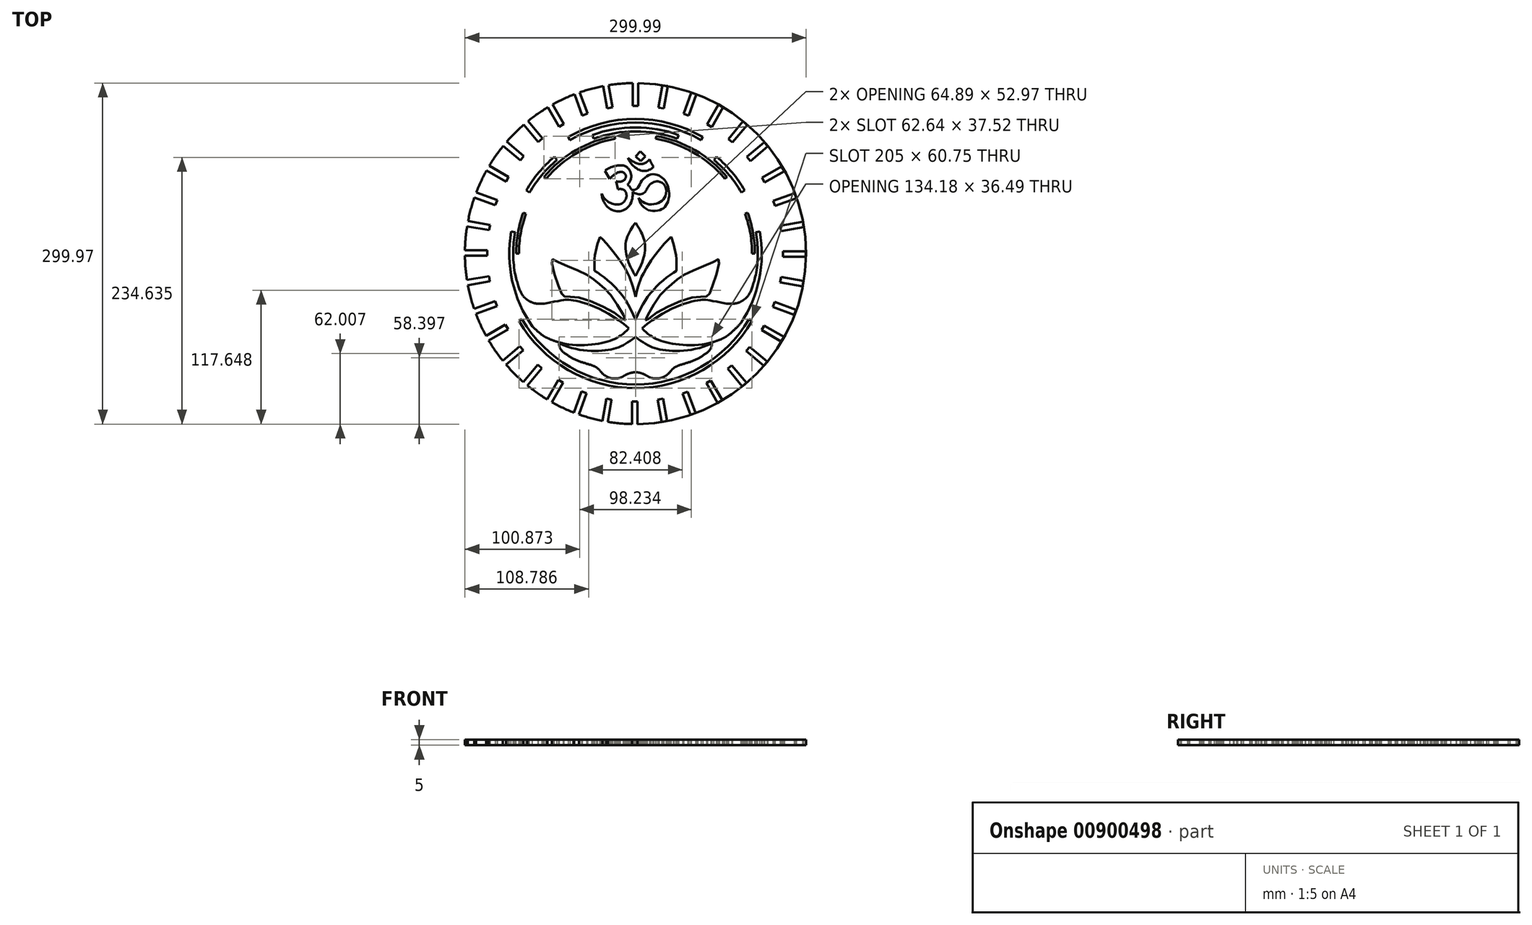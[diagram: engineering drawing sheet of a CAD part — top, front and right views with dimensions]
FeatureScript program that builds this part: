
annotation { "Feature Type Name" : "Feature", "Feature Type Description" : "" }
export const myFeature = defineFeature(function(context is Context, id is Id, definition is map)
    precondition{}
    {
        {
            var Q0;
            Q0=qCreatedBy(makeId("Top.planeOp"),FACE);
            var sketch = newSketch(context, id + "F0", { "sketchPlane" : qUnion([Q0])});
            skCircle(sketch, "E0", {"center": v(0, 0) * mm, "radius": 150 * mm});
            skLineSegment(sketch, "E1", {"start": v(0, 0) * mm, "end": v(0, 150) * mm});
            skPoint(sketch, "E2", {"position": v(0, 150) * mm});
            skPoint(sketch, "E3", {"position": v(0, 130) * mm});
            skLineSegment(sketch, "E4", {"start": v(-2.38, 130) * mm, "end": v(2.38, 130) * mm});
            skLineSegment(sketch, "E5", {"start": v(-2.38, 150) * mm, "end": v(2.37, 150) * mm});
            skLineSegment(sketch, "E6", {"start": v(-2.38, 150) * mm, "end": v(-2.38, 130) * mm});
            skLineSegment(sketch, "E7", {"start": v(2.38, 150) * mm, "end": v(2.38, 130) * mm});
            skLineSegment(sketch, "E8.1.0", {"start": v(-28.4, 147.38) * mm, "end": v(-24.92, 127.68) * mm});
            skLineSegment(sketch, "E8.1.1", {"start": v(-23.71, 148.2) * mm, "end": v(-20.24, 128.5) * mm});
            skLineSegment(sketch, "E8.1.2", {"start": v(-28.4, 147.38) * mm, "end": v(-23.71, 148.2) * mm});
            skLineSegment(sketch, "E8.1.3", {"start": v(-24.92, 127.68) * mm, "end": v(-20.24, 128.5) * mm});
            skLineSegment(sketch, "E8.2.0", {"start": v(-53.56, 140.27) * mm, "end": v(-46.72, 121.48) * mm});
            skLineSegment(sketch, "E8.2.1", {"start": v(-49.1, 141.9) * mm, "end": v(-42.25, 123.1) * mm});
            skLineSegment(sketch, "E8.2.2", {"start": v(-53.56, 140.27) * mm, "end": v(-49.1, 141.9) * mm});
            skLineSegment(sketch, "E8.2.3", {"start": v(-46.72, 121.48) * mm, "end": v(-42.25, 123.1) * mm});
            skLineSegment(sketch, "E8.3.0", {"start": v(-77.1, 128.91) * mm, "end": v(-67.1, 111.6) * mm});
            skLineSegment(sketch, "E8.3.1", {"start": v(-73, 131.29) * mm, "end": v(-63, 113.97) * mm});
            skLineSegment(sketch, "E8.3.2", {"start": v(-77.1, 128.91) * mm, "end": v(-73, 131.29) * mm});
            skLineSegment(sketch, "E8.3.3", {"start": v(-67.1, 111.6) * mm, "end": v(-63, 113.97) * mm});
            skLineSegment(sketch, "E8.4.0", {"start": v(-98.33, 113.63) * mm, "end": v(-85.47, 98.3) * mm});
            skLineSegment(sketch, "E8.4.1", {"start": v(-94.69, 116.68) * mm, "end": v(-81.83, 101.36) * mm});
            skLineSegment(sketch, "E8.4.2", {"start": v(-98.33, 113.63) * mm, "end": v(-94.69, 116.68) * mm});
            skLineSegment(sketch, "E8.4.3", {"start": v(-85.47, 98.3) * mm, "end": v(-81.83, 101.36) * mm});
            skLineSegment(sketch, "E8.5.0", {"start": v(-116.57, 94.9) * mm, "end": v(-101.25, 82.04) * mm});
            skLineSegment(sketch, "E8.5.1", {"start": v(-113.52, 98.54) * mm, "end": v(-98.2, 85.68) * mm});
            skLineSegment(sketch, "E8.5.2", {"start": v(-116.57, 94.9) * mm, "end": v(-113.52, 98.54) * mm});
            skLineSegment(sketch, "E8.5.3", {"start": v(-101.25, 82.04) * mm, "end": v(-98.2, 85.68) * mm});
            skLineSegment(sketch, "E8.6.0", {"start": v(-131.29, 73.28) * mm, "end": v(-113.97, 63.28) * mm});
            skLineSegment(sketch, "E8.6.1", {"start": v(-128.91, 77.4) * mm, "end": v(-111.6, 67.4) * mm});
            skLineSegment(sketch, "E8.6.2", {"start": v(-131.29, 73.28) * mm, "end": v(-128.91, 77.4) * mm});
            skLineSegment(sketch, "E8.6.3", {"start": v(-113.97, 63.28) * mm, "end": v(-111.6, 67.4) * mm});
            skLineSegment(sketch, "E8.7.0", {"start": v(-142.02, 49.44) * mm, "end": v(-123.23, 42.6) * mm});
            skLineSegment(sketch, "E8.7.1", {"start": v(-140.4, 53.9) * mm, "end": v(-121.6, 47.06) * mm});
            skLineSegment(sketch, "E8.7.2", {"start": v(-142.02, 49.44) * mm, "end": v(-140.4, 53.9) * mm});
            skLineSegment(sketch, "E8.7.3", {"start": v(-123.23, 42.6) * mm, "end": v(-121.6, 47.06) * mm});
            skLineSegment(sketch, "E8.8.0", {"start": v(-148.45, 24.1) * mm, "end": v(-128.76, 20.62) * mm});
            skLineSegment(sketch, "E8.8.1", {"start": v(-147.63, 28.77) * mm, "end": v(-127.93, 25.3) * mm});
            skLineSegment(sketch, "E8.8.2", {"start": v(-148.45, 24.1) * mm, "end": v(-147.63, 28.77) * mm});
            skLineSegment(sketch, "E8.8.3", {"start": v(-128.76, 20.62) * mm, "end": v(-127.93, 25.3) * mm});
            skLineSegment(sketch, "E8.9.0", {"start": v(-150.39, -1.99) * mm, "end": v(-130.39, -1.99) * mm});
            skLineSegment(sketch, "E8.9.1", {"start": v(-150.39, 2.76) * mm, "end": v(-130.39, 2.76) * mm});
            skLineSegment(sketch, "E8.9.2", {"start": v(-150.39, -1.99) * mm, "end": v(-150.39, 2.76) * mm});
            skLineSegment(sketch, "E8.9.3", {"start": v(-130.39, -1.99) * mm, "end": v(-130.39, 2.76) * mm});
            skLineSegment(sketch, "E8.10.0", {"start": v(-147.77, -28) * mm, "end": v(-128.07, -24.53) * mm});
            skLineSegment(sketch, "E8.10.1", {"start": v(-148.59, -23.33) * mm, "end": v(-128.9, -19.85) * mm});
            skLineSegment(sketch, "E8.10.2", {"start": v(-147.77, -28) * mm, "end": v(-148.59, -23.33) * mm});
            skLineSegment(sketch, "E8.10.3", {"start": v(-128.07, -24.53) * mm, "end": v(-128.9, -19.85) * mm});
            skLineSegment(sketch, "E8.11.0", {"start": v(-140.66, -53.17) * mm, "end": v(-121.87, -46.33) * mm});
            skLineSegment(sketch, "E8.11.1", {"start": v(-142.29, -48.7) * mm, "end": v(-123.5, -41.87) * mm});
            skLineSegment(sketch, "E8.11.2", {"start": v(-140.66, -53.17) * mm, "end": v(-142.29, -48.7) * mm});
            skLineSegment(sketch, "E8.11.3", {"start": v(-121.87, -46.33) * mm, "end": v(-123.5, -41.87) * mm});
            skLineSegment(sketch, "E8.12.0", {"start": v(-129.3, -76.72) * mm, "end": v(-111.98, -66.72) * mm});
            skLineSegment(sketch, "E8.12.1", {"start": v(-131.67, -72.6) * mm, "end": v(-114.35, -62.6) * mm});
            skLineSegment(sketch, "E8.12.2", {"start": v(-129.3, -76.72) * mm, "end": v(-131.67, -72.6) * mm});
            skLineSegment(sketch, "E8.12.3", {"start": v(-111.98, -66.72) * mm, "end": v(-114.35, -62.6) * mm});
            skLineSegment(sketch, "E8.13.0", {"start": v(-114.02, -97.94) * mm, "end": v(-98.7, -85.08) * mm});
            skLineSegment(sketch, "E8.13.1", {"start": v(-117.07, -94.3) * mm, "end": v(-101.75, -81.45) * mm});
            skLineSegment(sketch, "E8.13.2", {"start": v(-114.02, -97.94) * mm, "end": v(-117.07, -94.3) * mm});
            skLineSegment(sketch, "E8.13.3", {"start": v(-98.7, -85.08) * mm, "end": v(-101.75, -81.45) * mm});
            skLineSegment(sketch, "E8.14.0", {"start": v(-95.29, -116.18) * mm, "end": v(-82.43, -100.86) * mm});
            skLineSegment(sketch, "E8.14.1", {"start": v(-98.92, -113.13) * mm, "end": v(-86.07, -97.8) * mm});
            skLineSegment(sketch, "E8.14.2", {"start": v(-95.29, -116.18) * mm, "end": v(-98.92, -113.13) * mm});
            skLineSegment(sketch, "E8.14.3", {"start": v(-82.43, -100.86) * mm, "end": v(-86.07, -97.8) * mm});
            skLineSegment(sketch, "E8.15.0", {"start": v(-73.67, -130.9) * mm, "end": v(-63.67, -113.58) * mm});
            skLineSegment(sketch, "E8.15.1", {"start": v(-77.78, -128.52) * mm, "end": v(-67.78, -111.2) * mm});
            skLineSegment(sketch, "E8.15.2", {"start": v(-73.67, -130.9) * mm, "end": v(-77.78, -128.52) * mm});
            skLineSegment(sketch, "E8.15.3", {"start": v(-63.67, -113.58) * mm, "end": v(-67.78, -111.2) * mm});
            skLineSegment(sketch, "E8.16.0", {"start": v(-49.83, -141.63) * mm, "end": v(-42.99, -122.84) * mm});
            skLineSegment(sketch, "E8.16.1", {"start": v(-54.29, -140) * mm, "end": v(-47.45, -121.21) * mm});
            skLineSegment(sketch, "E8.16.2", {"start": v(-49.83, -141.63) * mm, "end": v(-54.29, -140) * mm});
            skLineSegment(sketch, "E8.16.3", {"start": v(-42.99, -122.84) * mm, "end": v(-47.45, -121.21) * mm});
            skLineSegment(sketch, "E8.17.0", {"start": v(-24.48, -148.07) * mm, "end": v(-21, -128.37) * mm});
            skLineSegment(sketch, "E8.17.1", {"start": v(-29.16, -147.24) * mm, "end": v(-25.69, -127.55) * mm});
            skLineSegment(sketch, "E8.17.2", {"start": v(-24.48, -148.07) * mm, "end": v(-29.16, -147.24) * mm});
            skLineSegment(sketch, "E8.17.3", {"start": v(-21, -128.37) * mm, "end": v(-25.69, -127.55) * mm});
            skLineSegment(sketch, "E8.18.0", {"start": v(1.6, -150) * mm, "end": v(1.6, -130) * mm});
            skLineSegment(sketch, "E8.18.1", {"start": v(-3.15, -150) * mm, "end": v(-3.15, -130) * mm});
            skLineSegment(sketch, "E8.18.2", {"start": v(1.6, -150) * mm, "end": v(-3.15, -150) * mm});
            skLineSegment(sketch, "E8.18.3", {"start": v(1.6, -130) * mm, "end": v(-3.15, -130) * mm});
            skLineSegment(sketch, "E8.19.0", {"start": v(27.61, -147.38) * mm, "end": v(24.14, -127.68) * mm});
            skLineSegment(sketch, "E8.19.1", {"start": v(22.94, -148.2) * mm, "end": v(19.46, -128.5) * mm});
            skLineSegment(sketch, "E8.19.2", {"start": v(27.61, -147.38) * mm, "end": v(22.94, -148.2) * mm});
            skLineSegment(sketch, "E8.19.3", {"start": v(24.14, -127.68) * mm, "end": v(19.46, -128.5) * mm});
            skLineSegment(sketch, "E8.20.0", {"start": v(52.78, -140.27) * mm, "end": v(45.94, -121.48) * mm});
            skLineSegment(sketch, "E8.20.1", {"start": v(48.32, -141.9) * mm, "end": v(41.48, -123.1) * mm});
            skLineSegment(sketch, "E8.20.2", {"start": v(52.78, -140.27) * mm, "end": v(48.32, -141.9) * mm});
            skLineSegment(sketch, "E8.20.3", {"start": v(45.94, -121.48) * mm, "end": v(41.48, -123.1) * mm});
            skLineSegment(sketch, "E8.21.0", {"start": v(76.33, -128.91) * mm, "end": v(66.33, -111.6) * mm});
            skLineSegment(sketch, "E8.21.1", {"start": v(72.22, -131.29) * mm, "end": v(62.22, -113.97) * mm});
            skLineSegment(sketch, "E8.21.2", {"start": v(76.33, -128.91) * mm, "end": v(72.22, -131.29) * mm});
            skLineSegment(sketch, "E8.21.3", {"start": v(66.33, -111.6) * mm, "end": v(62.22, -113.97) * mm});
            skLineSegment(sketch, "E8.22.0", {"start": v(97.55, -113.63) * mm, "end": v(84.7, -98.3) * mm});
            skLineSegment(sketch, "E8.22.1", {"start": v(93.91, -116.68) * mm, "end": v(81.06, -101.36) * mm});
            skLineSegment(sketch, "E8.22.2", {"start": v(97.55, -113.63) * mm, "end": v(93.91, -116.68) * mm});
            skLineSegment(sketch, "E8.22.3", {"start": v(84.7, -98.3) * mm, "end": v(81.06, -101.36) * mm});
            skLineSegment(sketch, "E8.23.0", {"start": v(115.8, -94.9) * mm, "end": v(100.47, -82.04) * mm});
            skLineSegment(sketch, "E8.23.1", {"start": v(112.74, -98.54) * mm, "end": v(97.42, -85.68) * mm});
            skLineSegment(sketch, "E8.23.2", {"start": v(115.8, -94.9) * mm, "end": v(112.74, -98.54) * mm});
            skLineSegment(sketch, "E8.23.3", {"start": v(100.47, -82.04) * mm, "end": v(97.42, -85.68) * mm});
            skLineSegment(sketch, "E8.24.0", {"start": v(130.5, -73.28) * mm, "end": v(113.19, -63.28) * mm});
            skLineSegment(sketch, "E8.24.1", {"start": v(128.13, -77.4) * mm, "end": v(110.81, -67.4) * mm});
            skLineSegment(sketch, "E8.24.2", {"start": v(130.5, -73.28) * mm, "end": v(128.13, -77.4) * mm});
            skLineSegment(sketch, "E8.24.3", {"start": v(113.19, -63.28) * mm, "end": v(110.81, -67.4) * mm});
            skLineSegment(sketch, "E8.25.0", {"start": v(141.24, -49.44) * mm, "end": v(122.45, -42.6) * mm});
            skLineSegment(sketch, "E8.25.1", {"start": v(139.62, -53.9) * mm, "end": v(120.83, -47.06) * mm});
            skLineSegment(sketch, "E8.25.2", {"start": v(141.24, -49.44) * mm, "end": v(139.62, -53.9) * mm});
            skLineSegment(sketch, "E8.25.3", {"start": v(122.45, -42.6) * mm, "end": v(120.83, -47.06) * mm});
            skLineSegment(sketch, "E8.26.0", {"start": v(147.68, -24.1) * mm, "end": v(127.98, -20.62) * mm});
            skLineSegment(sketch, "E8.26.1", {"start": v(146.85, -28.77) * mm, "end": v(127.16, -25.3) * mm});
            skLineSegment(sketch, "E8.26.2", {"start": v(147.68, -24.1) * mm, "end": v(146.85, -28.77) * mm});
            skLineSegment(sketch, "E8.26.3", {"start": v(127.98, -20.62) * mm, "end": v(127.16, -25.3) * mm});
            skLineSegment(sketch, "E8.27.0", {"start": v(149.61, 1.99) * mm, "end": v(129.61, 1.99) * mm});
            skLineSegment(sketch, "E8.27.1", {"start": v(149.61, -2.76) * mm, "end": v(129.61, -2.76) * mm});
            skLineSegment(sketch, "E8.27.2", {"start": v(149.61, 1.99) * mm, "end": v(149.61, -2.76) * mm});
            skLineSegment(sketch, "E8.27.3", {"start": v(129.61, 1.99) * mm, "end": v(129.61, -2.76) * mm});
            skLineSegment(sketch, "E8.28.0", {"start": v(146.99, 28) * mm, "end": v(127.3, 24.53) * mm});
            skLineSegment(sketch, "E8.28.1", {"start": v(147.81, 23.33) * mm, "end": v(128.12, 19.85) * mm});
            skLineSegment(sketch, "E8.28.2", {"start": v(146.99, 28) * mm, "end": v(147.81, 23.33) * mm});
            skLineSegment(sketch, "E8.28.3", {"start": v(127.3, 24.53) * mm, "end": v(128.12, 19.85) * mm});
            skLineSegment(sketch, "E8.29.0", {"start": v(139.89, 53.17) * mm, "end": v(121.1, 46.33) * mm});
            skLineSegment(sketch, "E8.29.1", {"start": v(141.51, 48.7) * mm, "end": v(122.72, 41.87) * mm});
            skLineSegment(sketch, "E8.29.2", {"start": v(139.89, 53.17) * mm, "end": v(141.51, 48.7) * mm});
            skLineSegment(sketch, "E8.29.3", {"start": v(121.1, 46.33) * mm, "end": v(122.72, 41.87) * mm});
            skLineSegment(sketch, "E8.30.0", {"start": v(128.52, 76.72) * mm, "end": v(111.2, 66.72) * mm});
            skLineSegment(sketch, "E8.30.1", {"start": v(130.9, 72.6) * mm, "end": v(113.58, 62.6) * mm});
            skLineSegment(sketch, "E8.30.2", {"start": v(128.52, 76.72) * mm, "end": v(130.9, 72.6) * mm});
            skLineSegment(sketch, "E8.30.3", {"start": v(111.2, 66.72) * mm, "end": v(113.58, 62.6) * mm});
            skLineSegment(sketch, "E8.31.0", {"start": v(113.24, 97.94) * mm, "end": v(97.92, 85.08) * mm});
            skLineSegment(sketch, "E8.31.1", {"start": v(116.3, 94.3) * mm, "end": v(100.97, 81.45) * mm});
            skLineSegment(sketch, "E8.31.2", {"start": v(113.24, 97.94) * mm, "end": v(116.3, 94.3) * mm});
            skLineSegment(sketch, "E8.31.3", {"start": v(97.92, 85.08) * mm, "end": v(100.97, 81.45) * mm});
            skLineSegment(sketch, "E8.32.0", {"start": v(94.5, 116.18) * mm, "end": v(81.65, 100.86) * mm});
            skLineSegment(sketch, "E8.32.1", {"start": v(98.15, 113.13) * mm, "end": v(85.3, 97.8) * mm});
            skLineSegment(sketch, "E8.32.2", {"start": v(94.5, 116.18) * mm, "end": v(98.15, 113.13) * mm});
            skLineSegment(sketch, "E8.32.3", {"start": v(81.65, 100.86) * mm, "end": v(85.3, 97.8) * mm});
            skLineSegment(sketch, "E8.33.0", {"start": v(72.9, 130.9) * mm, "end": v(62.9, 113.58) * mm});
            skLineSegment(sketch, "E8.33.1", {"start": v(77, 128.52) * mm, "end": v(67, 111.2) * mm});
            skLineSegment(sketch, "E8.33.2", {"start": v(72.9, 130.9) * mm, "end": v(77, 128.52) * mm});
            skLineSegment(sketch, "E8.33.3", {"start": v(62.9, 113.58) * mm, "end": v(67, 111.2) * mm});
            skLineSegment(sketch, "E8.34.0", {"start": v(49.05, 141.63) * mm, "end": v(42.2, 122.84) * mm});
            skLineSegment(sketch, "E8.34.1", {"start": v(53.51, 140) * mm, "end": v(46.67, 121.21) * mm});
            skLineSegment(sketch, "E8.34.2", {"start": v(49.05, 141.63) * mm, "end": v(53.51, 140) * mm});
            skLineSegment(sketch, "E8.34.3", {"start": v(42.2, 122.84) * mm, "end": v(46.67, 121.21) * mm});
            skLineSegment(sketch, "E8.35.0", {"start": v(23.7, 148.07) * mm, "end": v(20.23, 128.37) * mm});
            skLineSegment(sketch, "E8.35.1", {"start": v(28.38, 147.24) * mm, "end": v(24.9, 127.55) * mm});
            skLineSegment(sketch, "E8.35.2", {"start": v(23.7, 148.07) * mm, "end": v(28.38, 147.24) * mm});
            skLineSegment(sketch, "E8.35.3", {"start": v(20.23, 128.37) * mm, "end": v(24.9, 127.55) * mm});
            skPoint(sketch, "E8.center", {"position": v(-0.39, 0) * mm});
            skSolve(sketch);
        }
        {
            var Q0;
            {var subQ93=sQuery(id+"F0.wireOp",EDGE,"E8.1.3");Q0=makeQuery(id+"F0.imprint","IMPRINT",FACE,{"disambiguationData":[TD([[makeQuery(id+"F0.imprint","IMPRINT",EDGE,{"derivedFrom":subQ93}),-1.0]])]});}
            extrude(context, id + "F1", {"entities" : qUnion([Q0]), "depth" : 5 * mm, "offsetDistance" : 25 * mm});
        }
        {
            var Q0;
            Q0=qCreatedBy(makeId("Top.planeOp"),FACE);
            var sketch = newSketch(context, id + "F2", { "sketchPlane" : qUnion([Q0])});
            skCircle(sketch, "E9", {"center": v(0, 0) * mm, "radius": 111 * mm});
            skCircle(sketch, "E10", {"center": v(0, 0) * mm, "radius": 107.5 * mm});
            skFitSpline(sketch, "E11", {"points": [v(0, 27.16) * mm, v(-8.85, 6.85) * mm, v(0, -19.68) * mm], "startDerivative": vector(-25.73, -34.42) * mm, "endDerivative": vector(24.31, -38.78) * mm});
            skFitSpline(sketch, "E12", {"points": [v(0, 27.16) * mm, v(8.46, 6.43) * mm, v(0, -19.68) * mm], "startDerivative": vector(35.13, -51.75) * mm, "endDerivative": vector(-33.5, -59.16) * mm});
            skLineSegment(sketch, "E13", {"start": v(-31.43, 14.3) * mm, "end": v(-33.4, 8.36) * mm});
            skLineSegment(sketch, "E14", {"start": v(-33.4, 8.36) * mm, "end": v(-34.14, 5.43) * mm});
            skLineSegment(sketch, "E15", {"start": v(-34.14, 5.43) * mm, "end": v(-34.88, 1.99) * mm});
            skLineSegment(sketch, "E16", {"start": v(-34.88, 1.99) * mm, "end": v(-35.6, -1.45) * mm});
            skLineSegment(sketch, "E17", {"start": v(-35.6, -1.45) * mm, "end": v(-36.05, -4.75) * mm});
            skLineSegment(sketch, "E18", {"start": v(-36.05, -4.75) * mm, "end": v(-36.05, -8.11) * mm});
            skLineSegment(sketch, "E19", {"start": v(-36.05, -8.11) * mm, "end": v(-36.05, -15.14) * mm});
            skLineSegment(sketch, "E20", {"start": v(-36.05, -15.14) * mm, "end": v(-33.34, -16.87) * mm});
            skLineSegment(sketch, "E21", {"start": v(-33.34, -16.87) * mm, "end": v(-30.32, -18.87) * mm});
            skLineSegment(sketch, "E22", {"start": v(-30.32, -18.87) * mm, "end": v(-27.49, -21.03) * mm});
            skLineSegment(sketch, "E23", {"start": v(-27.49, -21.03) * mm, "end": v(-24.56, -23.37) * mm});
            skLineSegment(sketch, "E24", {"start": v(-24.56, -23.37) * mm, "end": v(-21.08, -26.42) * mm});
            skLineSegment(sketch, "E25", {"start": v(-21.08, -26.42) * mm, "end": v(-18.28, -29.2) * mm});
            skLineSegment(sketch, "E26", {"start": v(-18.28, -29.2) * mm, "end": v(-15.23, -32.64) * mm});
            skLineSegment(sketch, "E27", {"start": v(-15.23, -32.64) * mm, "end": v(-13.25, -34.98) * mm});
            skLineSegment(sketch, "E28", {"start": v(-13.25, -34.98) * mm, "end": v(-10.73, -38.1) * mm});
            skLineSegment(sketch, "E29", {"start": v(-10.73, -38.1) * mm, "end": v(-8.57, -41.3) * mm});
            skLineSegment(sketch, "E30", {"start": v(-8.57, -41.3) * mm, "end": v(-6.5, -44.56) * mm});
            skLineSegment(sketch, "E31", {"start": v(-6.5, -44.56) * mm, "end": v(-3.9, -49.34) * mm});
            skLineSegment(sketch, "E32", {"start": v(-3.9, -49.34) * mm, "end": v(-0.2, -57.75) * mm});
            skLineSegment(sketch, "E33", {"start": v(-0.2, -57.75) * mm, "end": v(0, -58.4) * mm});
            skLineSegment(sketch, "E34", {"start": v(0, -58.4) * mm, "end": v(0, -38.02) * mm});
            skLineSegment(sketch, "E35", {"start": v(0, -38.02) * mm, "end": v(-1.1, -33.22) * mm});
            skLineSegment(sketch, "E36", {"start": v(-1.1, -33.22) * mm, "end": v(-2.4, -28.72) * mm});
            skLineSegment(sketch, "E37", {"start": v(-2.4, -28.72) * mm, "end": v(-5.3, -20.65) * mm});
            skLineSegment(sketch, "E38", {"start": v(-5.3, -20.65) * mm, "end": v(-6.95, -17.48) * mm});
            skLineSegment(sketch, "E39", {"start": v(-6.95, -17.48) * mm, "end": v(-9.52, -12.79) * mm});
            skLineSegment(sketch, "E40", {"start": v(-9.52, -12.79) * mm, "end": v(-13.79, -6.03) * mm});
            skLineSegment(sketch, "E41", {"start": v(-13.79, -6.03) * mm, "end": v(-16.4, -2.42) * mm});
            skLineSegment(sketch, "E42", {"start": v(-16.4, -2.42) * mm, "end": v(-21.08, 3.66) * mm});
            skLineSegment(sketch, "E43", {"start": v(-21.08, 3.66) * mm, "end": v(-25.24, 8.56) * mm});
            skLineSegment(sketch, "E44", {"start": v(-25.24, 8.56) * mm, "end": v(-29.2, 12.65) * mm});
            skLineSegment(sketch, "E45", {"start": v(-29.2, 12.65) * mm, "end": v(-30.83, 14.3) * mm});
            skLineSegment(sketch, "E46", {"start": v(-30.83, 14.3) * mm, "end": v(-31.27, 14.67) * mm});
            skLineSegment(sketch, "E47", {"start": v(-31.27, 14.67) * mm, "end": v(-31.43, 14.3) * mm});
            skFitSpline(sketch, "E48", {"points": [v(-8.76, -58.83) * mm, v(-20.43, -38.43) * mm, v(-32.03, -26.6) * mm, v(-45.1, -17.5) * mm, v(-69.5, -6.7) * mm, v(-73.57, -5.6) * mm, v(-66.8, -31.25) * mm, v(-62.6, -37.76) * mm, v(-51.53, -38.48) * mm, v(-15.8, -54.02) * mm, v(-8.76, -58.83) * mm]});
            skFitSpline(sketch, "E49", {"points": [v(-106.18, -16.8) * mm, v(-96, -40.08) * mm, v(-80.27, -43.95) * mm], "startDerivative": vector(21.13, -88.18) * mm, "endDerivative": vector(53.61, 6.95) * mm});
            skFitSpline(sketch, "E50", {"points": [v(-80.27, -43.95) * mm, v(-56.73, -40.85) * mm, v(-5.75, -65.72) * mm], "startDerivative": vector(127.03, 21.81) * mm, "endDerivative": vector(104.18, -89.96) * mm});
            skFitSpline(sketch, "E51", {"points": [v(-5.75, -65.72) * mm, v(-26.18, -77.8) * mm, v(-77.81, -74.17) * mm], "startDerivative": vector(-47.22, -50.11) * mm, "endDerivative": vector(-92.2, 44.22) * mm});
            skFitSpline(sketch, "E52", {"points": [v(0, -73.35) * mm, v(-22.07, -84.34) * mm, v(-66.98, -78.99) * mm], "startDerivative": vector(-59.06, -45.69) * mm, "endDerivative": vector(-85.12, 40.5) * mm});
            skFitSpline(sketch, "E53", {"points": [v(-66.98, -78.99) * mm, v(-56.07, -91.81) * mm, v(-38.26, -98.26) * mm], "startDerivative": vector(-6.13, -31.6) * mm, "endDerivative": vector(34.17, -10.68) * mm});
            skFitSpline(sketch, "E54", {"points": [v(-38.26, -98.26) * mm, v(-30.64, -103.76) * mm, v(-20.67, -109.76) * mm], "startDerivative": vector(31.88, -12.84) * mm, "endDerivative": vector(30.88, -6.26) * mm});
            skFitSpline(sketch, "E55", {"points": [v(-20.67, -109.76) * mm, v(-11.44, -108.3) * mm, v(0, -104.27) * mm], "startDerivative": vector(33.39, -1.88) * mm, "endDerivative": vector(35.57, 3.3) * mm});
            skLineSegment(sketch, "E56.MirrorCS", {"start": v(30.83, 14.3) * mm, "end": v(31.27, 14.67) * mm});
            skLineSegment(sketch, "E57.MirrorCS", {"start": v(31.27, 14.67) * mm, "end": v(31.43, 14.3) * mm});
            skLineSegment(sketch, "E58.MirrorCS", {"start": v(29.2, 12.65) * mm, "end": v(30.83, 14.3) * mm});
            skLineSegment(sketch, "E59.MirrorCS", {"start": v(36.05, -4.75) * mm, "end": v(36.05, -8.11) * mm});
            skLineSegment(sketch, "E60.MirrorCS", {"start": v(35.6, -1.45) * mm, "end": v(36.05, -4.75) * mm});
            skLineSegment(sketch, "E61.MirrorCS", {"start": v(27.49, -21.03) * mm, "end": v(24.56, -23.37) * mm});
            skLineSegment(sketch, "E62.MirrorCS", {"start": v(34.14, 5.43) * mm, "end": v(34.88, 1.99) * mm});
            skLineSegment(sketch, "E63.MirrorCS", {"start": v(21.08, -26.42) * mm, "end": v(18.28, -29.2) * mm});
            skLineSegment(sketch, "E64.MirrorCS", {"start": v(25.24, 8.56) * mm, "end": v(29.2, 12.65) * mm});
            skLineSegment(sketch, "E65.MirrorCS", {"start": v(34.88, 1.99) * mm, "end": v(35.6, -1.45) * mm});
            skLineSegment(sketch, "E66.MirrorCS", {"start": v(33.4, 8.36) * mm, "end": v(34.14, 5.43) * mm});
            skLineSegment(sketch, "E67.MirrorCS", {"start": v(30.32, -18.87) * mm, "end": v(27.49, -21.03) * mm});
            skLineSegment(sketch, "E68.MirrorCS", {"start": v(33.34, -16.87) * mm, "end": v(30.32, -18.87) * mm});
            skLineSegment(sketch, "E69.MirrorCS", {"start": v(24.56, -23.37) * mm, "end": v(21.08, -26.42) * mm});
            skLineSegment(sketch, "E70.MirrorCS", {"start": v(21.08, 3.66) * mm, "end": v(25.24, 8.56) * mm});
            skLineSegment(sketch, "E71.MirrorCS", {"start": v(36.05, -15.14) * mm, "end": v(33.34, -16.87) * mm});
            skLineSegment(sketch, "E72.MirrorCS", {"start": v(18.28, -29.2) * mm, "end": v(15.23, -32.64) * mm});
            skLineSegment(sketch, "E73.MirrorCS", {"start": v(31.43, 14.3) * mm, "end": v(33.4, 8.36) * mm});
            skLineSegment(sketch, "E74.MirrorCS", {"start": v(16.4, -2.42) * mm, "end": v(21.08, 3.66) * mm});
            skLineSegment(sketch, "E75.MirrorCS", {"start": v(36.05, -8.11) * mm, "end": v(36.05, -15.14) * mm});
            skLineSegment(sketch, "E76.MirrorCS", {"start": v(9.52, -12.79) * mm, "end": v(13.79, -6.03) * mm});
            skLineSegment(sketch, "E77.MirrorCS", {"start": v(13.79, -6.03) * mm, "end": v(16.4, -2.42) * mm});
            skLineSegment(sketch, "E78.MirrorCS", {"start": v(6.95, -17.48) * mm, "end": v(9.52, -12.79) * mm});
            skLineSegment(sketch, "E79.MirrorCS", {"start": v(5.3, -20.65) * mm, "end": v(6.95, -17.48) * mm});
            skLineSegment(sketch, "E80.MirrorCS", {"start": v(2.4, -28.72) * mm, "end": v(5.3, -20.65) * mm});
            skLineSegment(sketch, "E81.MirrorCS", {"start": v(1.1, -33.22) * mm, "end": v(2.4, -28.72) * mm});
            skLineSegment(sketch, "E82.MirrorCS", {"start": v(0, -38.02) * mm, "end": v(1.1, -33.22) * mm});
            skFitSpline(sketch, "E83.MirrorC", {"points": [v(8.76, -58.83) * mm, v(20.43, -38.43) * mm, v(32.03, -26.6) * mm, v(45.1, -17.5) * mm, v(69.5, -6.7) * mm, v(73.57, -5.6) * mm, v(66.8, -31.25) * mm, v(62.6, -37.76) * mm, v(51.53, -38.48) * mm, v(15.8, -54.02) * mm, v(8.76, -58.83) * mm]});
            skLineSegment(sketch, "E84.MirrorCS", {"start": v(3.9, -49.34) * mm, "end": v(0.2, -57.75) * mm});
            skLineSegment(sketch, "E85.MirrorCS", {"start": v(6.5, -44.56) * mm, "end": v(3.9, -49.34) * mm});
            skLineSegment(sketch, "E86.MirrorCS", {"start": v(8.57, -41.3) * mm, "end": v(6.5, -44.56) * mm});
            skLineSegment(sketch, "E87.MirrorCS", {"start": v(10.73, -38.1) * mm, "end": v(8.57, -41.3) * mm});
            skLineSegment(sketch, "E88.MirrorCS", {"start": v(13.25, -34.98) * mm, "end": v(10.73, -38.1) * mm});
            skLineSegment(sketch, "E89.MirrorCS", {"start": v(15.23, -32.64) * mm, "end": v(13.25, -34.98) * mm});
            skFitSpline(sketch, "E90.MirrorCS", {"points": [v(80.27, -43.95) * mm, v(56.73, -40.85) * mm, v(5.75, -65.72) * mm], "startDerivative": vector(-127.03, 21.81) * mm, "endDerivative": vector(-104.18, -89.96) * mm});
            skFitSpline(sketch, "E91.MirrorCS", {"points": [v(106.18, -16.8) * mm, v(96, -40.08) * mm, v(80.27, -43.95) * mm], "startDerivative": vector(-21.13, -88.18) * mm, "endDerivative": vector(-53.61, 6.95) * mm});
            skFitSpline(sketch, "E92.MirrorCS", {"points": [v(5.75, -65.72) * mm, v(26.18, -77.8) * mm, v(77.81, -74.17) * mm], "startDerivative": vector(47.22, -50.11) * mm, "endDerivative": vector(92.2, 44.22) * mm});
            skFitSpline(sketch, "E93.MirrorCS", {"points": [v(0, -73.35) * mm, v(22.07, -84.34) * mm, v(66.98, -78.99) * mm], "startDerivative": vector(59.06, -45.69) * mm, "endDerivative": vector(85.12, 40.5) * mm});
            skFitSpline(sketch, "E94.MirrorCS", {"points": [v(66.98, -78.99) * mm, v(56.07, -91.81) * mm, v(38.26, -98.26) * mm], "startDerivative": vector(6.13, -31.6) * mm, "endDerivative": vector(-34.17, -10.68) * mm});
            skFitSpline(sketch, "E95.MirrorCS", {"points": [v(38.26, -98.26) * mm, v(30.64, -103.76) * mm, v(20.67, -109.76) * mm], "startDerivative": vector(-31.88, -12.84) * mm, "endDerivative": vector(-30.88, -6.26) * mm});
            skFitSpline(sketch, "E96.MirrorCS", {"points": [v(20.67, -109.76) * mm, v(11.44, -108.3) * mm, v(0, -104.27) * mm], "startDerivative": vector(-33.39, -1.88) * mm, "endDerivative": vector(-35.57, 3.3) * mm});
            skLineSegment(sketch, "E97", {"start": v(0.2, -57.75) * mm, "end": v(0, -58.4) * mm});
            skFitSpline(sketch, "E98", {"points": [v(-26.7, 72.77) * mm, v(-13.42, 77.6) * mm, v(-6.5, 75.18) * mm], "startDerivative": vector(21.8, 19.32) * mm, "endDerivative": vector(14.95, -14.34) * mm});
            skFitSpline(sketch, "E99", {"points": [v(-6.5, 75.18) * mm, v(-3.7, 68.3) * mm, v(-7.26, 60.5) * mm], "startDerivative": vector(9.95, -14.52) * mm, "endDerivative": vector(-14.74, -12.4) * mm});
            skFitSpline(sketch, "E100", {"points": [v(-7.26, 60.5) * mm, v(-4.95, 58.59) * mm, v(-3.71, 56.33) * mm], "startDerivative": vector(4.89, -2) * mm, "endDerivative": vector(2.94, -5.43) * mm});
            skFitSpline(sketch, "E101", {"points": [v(-3.71, 56.33) * mm, v(-1.4, 55.95) * mm, v(2, 57.85) * mm], "startDerivative": vector(4.58, -2.7) * mm, "endDerivative": vector(5.06, 5.98) * mm});
            skFitSpline(sketch, "E102", {"points": [v(2, 57.85) * mm, v(6.84, 65.52) * mm, v(15.9, 69.8) * mm, v(23.4, 66.9) * mm, v(27.29, 62.25) * mm, v(29.08, 56.86) * mm], "startDerivative": vector(23.25, 36.12) * mm, "endDerivative": vector(8.27, -32.36) * mm});
            skFitSpline(sketch, "E103", {"points": [v(29.08, 56.86) * mm, v(29.6, 51.88) * mm, v(28.5, 45.65) * mm, v(26.67, 42.25) * mm, v(24.21, 39.64) * mm, v(20.84, 38.14) * mm, v(15.93, 37.48) * mm, v(11.02, 38.4) * mm, v(6.08, 42.03) * mm, v(3.84, 45.36) * mm, v(2.78, 49.02) * mm], "startDerivative": vector(7.55, -39.21) * mm, "endDerivative": vector(-9.57, 41.45) * mm});
            skFitSpline(sketch, "E104", {"points": [v(2.78, 49.02) * mm, v(5.16, 46.46) * mm, v(8.46, 44.3) * mm, v(12.93, 43.2) * mm, v(18.28, 43.97) * mm, v(22.34, 45.84) * mm, v(25.2, 48.66) * mm, v(26.81, 52.5) * mm, v(26.6, 57.85) * mm, v(23.84, 62) * mm, v(19.81, 63.53) * mm], "startDerivative": vector(25.23, -29.93) * mm, "endDerivative": vector(-50.97, 8.47) * mm});
            skFitSpline(sketch, "E105", {"points": [v(19.81, 63.53) * mm, v(16.19, 62.9) * mm, v(12.82, 60.9) * mm, v(10.22, 57.16) * mm, v(9.12, 55.07) * mm, v(7.21, 53.09) * mm, v(3.88, 52.14) * mm, v(0.62, 52.72) * mm, v(-2.57, 54.22) * mm], "startDerivative": vector(-24.2, 2.46) * mm, "endDerivative": vector(-23.31, 11.81) * mm});
            skFitSpline(sketch, "E106", {"points": [v(-2.57, 54.22) * mm, v(-2.57, 49.94) * mm, v(-3.71, 45.29) * mm, v(-6.18, 41.31) * mm, v(-8.8, 39.08) * mm, v(-12.55, 37.48) * mm, v(-16.57, 37.17) * mm, v(-20.78, 38.34) * mm, v(-24.63, 41.02) * mm], "startDerivative": vector(2.15, -32.97) * mm, "endDerivative": vector(-29.9, 24.1) * mm});
            skFitSpline(sketch, "E107", {"points": [v(-24.63, 41.02) * mm, v(-28.71, 47.5) * mm, v(-29.75, 52.61) * mm], "startDerivative": vector(-10, 10.42) * mm, "endDerivative": vector(-0.55, 11.33) * mm});
            skFitSpline(sketch, "E108", {"points": [v(-29.75, 52.61) * mm, v(-24.63, 46.1) * mm, v(-15.58, 43.09) * mm, v(-8, 49.54) * mm], "startDerivative": vector(11.4, -26.02) * mm, "endDerivative": vector(11.17, 38.64) * mm});
            skFitSpline(sketch, "E109", {"points": [v(-8, 49.54) * mm, v(-9.71, 55.54) * mm, v(-15.44, 56.62) * mm], "startDerivative": vector(2.34, 15.22) * mm, "endDerivative": vector(-18.18, -2.13) * mm});
            skFitSpline(sketch, "E110", {"points": [v(-15.44, 56.62) * mm, v(-17.06, 63.53) * mm], "startDerivative": vector(-1.61, 6.9) * mm, "endDerivative": vector(-1.61, 6.9) * mm});
            skFitSpline(sketch, "E111", {"points": [v(-17.06, 63.53) * mm, v(-13.29, 63.2) * mm, v(-9.2, 65.47) * mm, v(-8.67, 69.28) * mm], "startDerivative": vector(9.55, -2.47) * mm, "endDerivative": vector(-3.6, 12.97) * mm});
            skFitSpline(sketch, "E112", {"points": [v(-8.67, 69.28) * mm, v(-13.5, 71.86) * mm, v(-19.65, 68.63) * mm, v(-22.7, 65.68) * mm], "startDerivative": vector(-10.08, 17.77) * mm, "endDerivative": vector(-8.28, -9.42) * mm});
            skFitSpline(sketch, "E113", {"points": [v(-26.7, 72.77) * mm, v(-22.7, 65.68) * mm], "startDerivative": vector(4.04, -7.2) * mm, "endDerivative": vector(4.04, -7.2) * mm});
            skFitSpline(sketch, "E114", {"points": [v(-6.62, 84.14) * mm, v(3.8, 78.79) * mm, v(12.44, 82.8) * mm], "startDerivative": vector(18.15, -15.66) * mm, "endDerivative": vector(18.88, 20.67) * mm});
            skFitSpline(sketch, "E115", {"points": [v(12.44, 82.8) * mm, v(15.86, 76.35) * mm], "startDerivative": vector(3, -7.12) * mm, "endDerivative": vector(4.77, -6.6) * mm});
            skFitSpline(sketch, "E116", {"points": [v(15.86, 76.35) * mm, v(7.78, 72.66) * mm, v(-1.9, 77.04) * mm, v(-6.62, 84.14) * mm], "startDerivative": vector(-17.55, -19.16) * mm, "endDerivative": vector(-6.98, 20.11) * mm});
            skLineSegment(sketch, "E117", {"start": v(4.4, 89.9) * mm, "end": v(0.16, 85.54) * mm});
            skLineSegment(sketch, "E118", {"start": v(0.16, 85.54) * mm, "end": v(4.47, 81.33) * mm});
            skLineSegment(sketch, "E119", {"start": v(4.47, 81.33) * mm, "end": v(8.62, 85.6) * mm});
            skLineSegment(sketch, "E120", {"start": v(8.62, 85.6) * mm, "end": v(4.4, 89.9) * mm});
            skCircle(sketch, "E121", {"center": v(0, 0) * mm, "radius": 105 * mm});
            skCircle(sketch, "E122", {"center": v(0, 0) * mm, "radius": 102.5 * mm});
            skLineSegment(sketch, "E123", {"start": v(0, 105) * mm, "end": v(0, 102.5) * mm});
            skLineSegment(sketch, "E124.1.0", {"start": v(0.4, -110.6) * mm, "end": v(0.4, -107.1) * mm});
            skPoint(sketch, "E124.center", {"position": v(0.2, 0.2) * mm});
            skLineSegment(sketch, "E125.1.0", {"start": v(-18.23, 103.4) * mm, "end": v(-17.8, 100.94) * mm});
            skLineSegment(sketch, "E125.2.0", {"start": v(-35.91, 98.67) * mm, "end": v(-35.06, 96.32) * mm});
            skLineSegment(sketch, "E125.3.0", {"start": v(-52.5, 90.93) * mm, "end": v(-51.25, 88.77) * mm});
            skLineSegment(sketch, "E125.4.0", {"start": v(-67.5, 80.43) * mm, "end": v(-65.89, 78.52) * mm});
            skLineSegment(sketch, "E125.5.0", {"start": v(-80.43, 67.5) * mm, "end": v(-78.52, 65.89) * mm});
            skLineSegment(sketch, "E125.6.0", {"start": v(-90.93, 52.5) * mm, "end": v(-88.77, 51.25) * mm});
            skLineSegment(sketch, "E125.7.0", {"start": v(-98.67, 35.91) * mm, "end": v(-96.32, 35.06) * mm});
            skLineSegment(sketch, "E125.8.0", {"start": v(-103.4, 18.23) * mm, "end": v(-100.94, 17.8) * mm});
            skLineSegment(sketch, "E125.9.0", {"start": v(-105, 0) * mm, "end": v(-102.5, 0) * mm});
            skLineSegment(sketch, "E125.10.0", {"start": v(-103.4, -18.23) * mm, "end": v(-100.94, -17.8) * mm});
            skLineSegment(sketch, "E125.11.0", {"start": v(-98.67, -35.91) * mm, "end": v(-96.32, -35.06) * mm});
            skLineSegment(sketch, "E125.12.0", {"start": v(-90.93, -52.5) * mm, "end": v(-88.77, -51.25) * mm});
            skLineSegment(sketch, "E125.13.0", {"start": v(-80.43, -67.5) * mm, "end": v(-78.52, -65.89) * mm});
            skLineSegment(sketch, "E125.14.0", {"start": v(-67.5, -80.43) * mm, "end": v(-65.89, -78.52) * mm});
            skLineSegment(sketch, "E125.15.0", {"start": v(-52.5, -90.93) * mm, "end": v(-51.25, -88.77) * mm});
            skLineSegment(sketch, "E125.16.0", {"start": v(-35.91, -98.67) * mm, "end": v(-35.06, -96.32) * mm});
            skLineSegment(sketch, "E125.17.0", {"start": v(-18.23, -103.4) * mm, "end": v(-17.8, -100.94) * mm});
            skLineSegment(sketch, "E125.18.0", {"start": v(0, -105) * mm, "end": v(0, -102.5) * mm});
            skLineSegment(sketch, "E125.19.0", {"start": v(18.23, -103.4) * mm, "end": v(17.8, -100.94) * mm});
            skLineSegment(sketch, "E125.20.0", {"start": v(35.91, -98.67) * mm, "end": v(35.06, -96.32) * mm});
            skLineSegment(sketch, "E125.21.0", {"start": v(52.5, -90.93) * mm, "end": v(51.25, -88.77) * mm});
            skLineSegment(sketch, "E125.22.0", {"start": v(67.5, -80.43) * mm, "end": v(65.89, -78.52) * mm});
            skLineSegment(sketch, "E125.23.0", {"start": v(80.43, -67.5) * mm, "end": v(78.52, -65.89) * mm});
            skLineSegment(sketch, "E125.24.0", {"start": v(90.93, -52.5) * mm, "end": v(88.77, -51.25) * mm});
            skLineSegment(sketch, "E125.25.0", {"start": v(98.67, -35.91) * mm, "end": v(96.32, -35.06) * mm});
            skLineSegment(sketch, "E125.26.0", {"start": v(103.4, -18.23) * mm, "end": v(100.94, -17.8) * mm});
            skLineSegment(sketch, "E125.27.0", {"start": v(105, 0) * mm, "end": v(102.5, 0) * mm});
            skLineSegment(sketch, "E125.28.0", {"start": v(103.4, 18.23) * mm, "end": v(100.94, 17.8) * mm});
            skLineSegment(sketch, "E125.29.0", {"start": v(98.67, 35.91) * mm, "end": v(96.32, 35.06) * mm});
            skLineSegment(sketch, "E125.30.0", {"start": v(90.93, 52.5) * mm, "end": v(88.77, 51.25) * mm});
            skLineSegment(sketch, "E125.31.0", {"start": v(80.43, 67.5) * mm, "end": v(78.52, 65.89) * mm});
            skLineSegment(sketch, "E125.32.0", {"start": v(67.5, 80.43) * mm, "end": v(65.89, 78.52) * mm});
            skLineSegment(sketch, "E125.33.0", {"start": v(52.5, 90.93) * mm, "end": v(51.25, 88.77) * mm});
            skLineSegment(sketch, "E125.34.0", {"start": v(35.91, 98.67) * mm, "end": v(35.06, 96.32) * mm});
            skLineSegment(sketch, "E125.35.0", {"start": v(18.23, 103.4) * mm, "end": v(17.8, 100.94) * mm});
            skLineSegment(sketch, "E126", {"start": v(0, 111) * mm, "end": v(0, 107.5) * mm});
            skLineSegment(sketch, "E127.1.0", {"start": v(-19.27, 109.31) * mm, "end": v(-18.67, 105.87) * mm});
            skLineSegment(sketch, "E127.2.0", {"start": v(-37.96, 104.3) * mm, "end": v(-36.77, 101.02) * mm});
            skLineSegment(sketch, "E127.3.0", {"start": v(-55.5, 96.13) * mm, "end": v(-53.75, 93.1) * mm});
            skLineSegment(sketch, "E127.4.0", {"start": v(-71.35, 85.03) * mm, "end": v(-69.1, 82.35) * mm});
            skLineSegment(sketch, "E127.5.0", {"start": v(-85.03, 71.35) * mm, "end": v(-82.35, 69.1) * mm});
            skLineSegment(sketch, "E127.6.0", {"start": v(-96.13, 55.5) * mm, "end": v(-93.1, 53.75) * mm});
            skLineSegment(sketch, "E127.7.0", {"start": v(-104.3, 37.96) * mm, "end": v(-101.02, 36.77) * mm});
            skLineSegment(sketch, "E127.8.0", {"start": v(-109.31, 19.27) * mm, "end": v(-105.87, 18.67) * mm});
            skLineSegment(sketch, "E127.9.0", {"start": v(-111, 0) * mm, "end": v(-107.5, 0) * mm});
            skLineSegment(sketch, "E127.10.0", {"start": v(-109.31, -19.27) * mm, "end": v(-105.87, -18.67) * mm});
            skLineSegment(sketch, "E127.11.0", {"start": v(-104.3, -37.96) * mm, "end": v(-101.02, -36.77) * mm});
            skLineSegment(sketch, "E127.12.0", {"start": v(-96.13, -55.5) * mm, "end": v(-93.1, -53.75) * mm});
            skLineSegment(sketch, "E127.13.0", {"start": v(-85.03, -71.35) * mm, "end": v(-82.35, -69.1) * mm});
            skLineSegment(sketch, "E127.14.0", {"start": v(-71.35, -85.03) * mm, "end": v(-69.1, -82.35) * mm});
            skLineSegment(sketch, "E127.15.0", {"start": v(-55.5, -96.13) * mm, "end": v(-53.75, -93.1) * mm});
            skLineSegment(sketch, "E127.16.0", {"start": v(-37.96, -104.3) * mm, "end": v(-36.77, -101.02) * mm});
            skLineSegment(sketch, "E127.17.0", {"start": v(-19.27, -109.31) * mm, "end": v(-18.67, -105.87) * mm});
            skLineSegment(sketch, "E127.18.0", {"start": v(0, -111) * mm, "end": v(0, -107.5) * mm});
            skLineSegment(sketch, "E127.19.0", {"start": v(19.27, -109.31) * mm, "end": v(18.67, -105.87) * mm});
            skLineSegment(sketch, "E127.20.0", {"start": v(37.96, -104.3) * mm, "end": v(36.77, -101.02) * mm});
            skLineSegment(sketch, "E127.21.0", {"start": v(55.5, -96.13) * mm, "end": v(53.75, -93.1) * mm});
            skLineSegment(sketch, "E127.22.0", {"start": v(71.35, -85.03) * mm, "end": v(69.1, -82.35) * mm});
            skLineSegment(sketch, "E127.23.0", {"start": v(85.03, -71.35) * mm, "end": v(82.35, -69.1) * mm});
            skLineSegment(sketch, "E127.24.0", {"start": v(96.13, -55.5) * mm, "end": v(93.1, -53.75) * mm});
            skLineSegment(sketch, "E127.25.0", {"start": v(104.3, -37.96) * mm, "end": v(101.02, -36.77) * mm});
            skLineSegment(sketch, "E127.26.0", {"start": v(109.31, -19.27) * mm, "end": v(105.87, -18.67) * mm});
            skLineSegment(sketch, "E127.27.0", {"start": v(111, 0) * mm, "end": v(107.5, 0) * mm});
            skLineSegment(sketch, "E127.28.0", {"start": v(109.31, 19.27) * mm, "end": v(105.87, 18.67) * mm});
            skLineSegment(sketch, "E127.29.0", {"start": v(104.3, 37.96) * mm, "end": v(101.02, 36.77) * mm});
            skLineSegment(sketch, "E127.30.0", {"start": v(96.13, 55.5) * mm, "end": v(93.1, 53.75) * mm});
            skLineSegment(sketch, "E127.31.0", {"start": v(85.03, 71.35) * mm, "end": v(82.35, 69.1) * mm});
            skLineSegment(sketch, "E127.32.0", {"start": v(71.35, 85.03) * mm, "end": v(69.1, 82.35) * mm});
            skLineSegment(sketch, "E127.33.0", {"start": v(55.5, 96.13) * mm, "end": v(53.75, 93.1) * mm});
            skLineSegment(sketch, "E127.34.0", {"start": v(37.96, 104.3) * mm, "end": v(36.77, 101.02) * mm});
            skLineSegment(sketch, "E127.35.0", {"start": v(19.27, 109.31) * mm, "end": v(18.67, 105.87) * mm});
            skFitSpline(sketch, "E128", {"points": [v(-77.81, -74.17) * mm, v(-90.57, -64.17) * mm], "startDerivative": vector(-9.85, 4.7) * mm, "endDerivative": vector(-19.48, 19.15) * mm});
            skFitSpline(sketch, "E129", {"points": [v(77.81, -74.17) * mm, v(92.72, -61.02) * mm], "startDerivative": vector(11.47, 6.9) * mm, "endDerivative": vector(20.32, 21.82) * mm});
            skSolve(sketch);
        }
        {
            var Q0;
            Q0=makeQuery(id+"F1.opExtrude","CAP_FACE",FACE,{"disambiguationData":[OSD([sQuery(id+"F0.wireOp",EDGE,"E0"),sQuery(id+"F0.wireOp",EDGE,"E4"),sQuery(id+"F0.wireOp",EDGE,"E6"),sQuery(id+"F0.wireOp",EDGE,"E7"),sQuery(id+"F0.wireOp",EDGE,"E8.1.0"),sQuery(id+"F0.wireOp",EDGE,"E8.1.1"),sQuery(id+"F0.wireOp",EDGE,"E8.1.3"),sQuery(id+"F0.wireOp",EDGE,"E8.2.0"),sQuery(id+"F0.wireOp",EDGE,"E8.2.1"),sQuery(id+"F0.wireOp",EDGE,"E8.2.3"),sQuery(id+"F0.wireOp",EDGE,"E8.3.0"),sQuery(id+"F0.wireOp",EDGE,"E8.3.1"),sQuery(id+"F0.wireOp",EDGE,"E8.3.3"),sQuery(id+"F0.wireOp",EDGE,"E8.4.0"),sQuery(id+"F0.wireOp",EDGE,"E8.4.1"),sQuery(id+"F0.wireOp",EDGE,"E8.4.3"),sQuery(id+"F0.wireOp",EDGE,"E8.5.0"),sQuery(id+"F0.wireOp",EDGE,"E8.5.1"),sQuery(id+"F0.wireOp",EDGE,"E8.5.3"),sQuery(id+"F0.wireOp",EDGE,"E8.6.0"),sQuery(id+"F0.wireOp",EDGE,"E8.6.1"),sQuery(id+"F0.wireOp",EDGE,"E8.6.3"),sQuery(id+"F0.wireOp",EDGE,"E8.7.0"),sQuery(id+"F0.wireOp",EDGE,"E8.7.1"),sQuery(id+"F0.wireOp",EDGE,"E8.7.3"),sQuery(id+"F0.wireOp",EDGE,"E8.8.0"),sQuery(id+"F0.wireOp",EDGE,"E8.8.1"),sQuery(id+"F0.wireOp",EDGE,"E8.8.3"),sQuery(id+"F0.wireOp",EDGE,"E8.9.0"),sQuery(id+"F0.wireOp",EDGE,"E8.9.1"),sQuery(id+"F0.wireOp",EDGE,"E8.9.3"),sQuery(id+"F0.wireOp",EDGE,"E8.10.0"),sQuery(id+"F0.wireOp",EDGE,"E8.10.1"),sQuery(id+"F0.wireOp",EDGE,"E8.10.3"),sQuery(id+"F0.wireOp",EDGE,"E8.11.0"),sQuery(id+"F0.wireOp",EDGE,"E8.11.1"),sQuery(id+"F0.wireOp",EDGE,"E8.11.3"),sQuery(id+"F0.wireOp",EDGE,"E8.12.0"),sQuery(id+"F0.wireOp",EDGE,"E8.12.1"),sQuery(id+"F0.wireOp",EDGE,"E8.12.3"),sQuery(id+"F0.wireOp",EDGE,"E8.13.0"),sQuery(id+"F0.wireOp",EDGE,"E8.13.1"),sQuery(id+"F0.wireOp",EDGE,"E8.13.3"),sQuery(id+"F0.wireOp",EDGE,"E8.14.0"),sQuery(id+"F0.wireOp",EDGE,"E8.14.1"),sQuery(id+"F0.wireOp",EDGE,"E8.14.3"),sQuery(id+"F0.wireOp",EDGE,"E8.15.0"),sQuery(id+"F0.wireOp",EDGE,"E8.15.1"),sQuery(id+"F0.wireOp",EDGE,"E8.15.3"),sQuery(id+"F0.wireOp",EDGE,"E8.16.0"),sQuery(id+"F0.wireOp",EDGE,"E8.16.1"),sQuery(id+"F0.wireOp",EDGE,"E8.16.3"),sQuery(id+"F0.wireOp",EDGE,"E8.17.0"),sQuery(id+"F0.wireOp",EDGE,"E8.17.1"),sQuery(id+"F0.wireOp",EDGE,"E8.17.3"),sQuery(id+"F0.wireOp",EDGE,"E8.18.0"),sQuery(id+"F0.wireOp",EDGE,"E8.18.1"),sQuery(id+"F0.wireOp",EDGE,"E8.18.3"),sQuery(id+"F0.wireOp",EDGE,"E8.19.0"),sQuery(id+"F0.wireOp",EDGE,"E8.19.1"),sQuery(id+"F0.wireOp",EDGE,"E8.19.2"),sQuery(id+"F0.wireOp",EDGE,"E8.19.3"),sQuery(id+"F0.wireOp",EDGE,"E8.20.0"),sQuery(id+"F0.wireOp",EDGE,"E8.20.1"),sQuery(id+"F0.wireOp",EDGE,"E8.20.2"),sQuery(id+"F0.wireOp",EDGE,"E8.20.3"),sQuery(id+"F0.wireOp",EDGE,"E8.21.0"),sQuery(id+"F0.wireOp",EDGE,"E8.21.1"),sQuery(id+"F0.wireOp",EDGE,"E8.21.2"),sQuery(id+"F0.wireOp",EDGE,"E8.21.3"),sQuery(id+"F0.wireOp",EDGE,"E8.22.0"),sQuery(id+"F0.wireOp",EDGE,"E8.22.1"),sQuery(id+"F0.wireOp",EDGE,"E8.22.2"),sQuery(id+"F0.wireOp",EDGE,"E8.22.3"),sQuery(id+"F0.wireOp",EDGE,"E8.23.0"),sQuery(id+"F0.wireOp",EDGE,"E8.23.1"),sQuery(id+"F0.wireOp",EDGE,"E8.23.2"),sQuery(id+"F0.wireOp",EDGE,"E8.23.3"),sQuery(id+"F0.wireOp",EDGE,"E8.24.0"),sQuery(id+"F0.wireOp",EDGE,"E8.24.1"),sQuery(id+"F0.wireOp",EDGE,"E8.24.2"),sQuery(id+"F0.wireOp",EDGE,"E8.24.3"),sQuery(id+"F0.wireOp",EDGE,"E8.25.0"),sQuery(id+"F0.wireOp",EDGE,"E8.25.1"),sQuery(id+"F0.wireOp",EDGE,"E8.25.2"),sQuery(id+"F0.wireOp",EDGE,"E8.25.3"),sQuery(id+"F0.wireOp",EDGE,"E8.26.0"),sQuery(id+"F0.wireOp",EDGE,"E8.26.1"),sQuery(id+"F0.wireOp",EDGE,"E8.26.2"),sQuery(id+"F0.wireOp",EDGE,"E8.26.3"),sQuery(id+"F0.wireOp",EDGE,"E8.27.0"),sQuery(id+"F0.wireOp",EDGE,"E8.27.1"),sQuery(id+"F0.wireOp",EDGE,"E8.27.2"),sQuery(id+"F0.wireOp",EDGE,"E8.27.3"),sQuery(id+"F0.wireOp",EDGE,"E8.28.0"),sQuery(id+"F0.wireOp",EDGE,"E8.28.1"),sQuery(id+"F0.wireOp",EDGE,"E8.28.2"),sQuery(id+"F0.wireOp",EDGE,"E8.28.3"),sQuery(id+"F0.wireOp",EDGE,"E8.29.0"),sQuery(id+"F0.wireOp",EDGE,"E8.29.1"),sQuery(id+"F0.wireOp",EDGE,"E8.29.2"),sQuery(id+"F0.wireOp",EDGE,"E8.29.3"),sQuery(id+"F0.wireOp",EDGE,"E8.30.0"),sQuery(id+"F0.wireOp",EDGE,"E8.30.1"),sQuery(id+"F0.wireOp",EDGE,"E8.30.2"),sQuery(id+"F0.wireOp",EDGE,"E8.30.3"),sQuery(id+"F0.wireOp",EDGE,"E8.31.0"),sQuery(id+"F0.wireOp",EDGE,"E8.31.1"),sQuery(id+"F0.wireOp",EDGE,"E8.31.2"),sQuery(id+"F0.wireOp",EDGE,"E8.31.3"),sQuery(id+"F0.wireOp",EDGE,"E8.32.0"),sQuery(id+"F0.wireOp",EDGE,"E8.32.1"),sQuery(id+"F0.wireOp",EDGE,"E8.32.2"),sQuery(id+"F0.wireOp",EDGE,"E8.32.3"),sQuery(id+"F0.wireOp",EDGE,"E8.33.0"),sQuery(id+"F0.wireOp",EDGE,"E8.33.1"),sQuery(id+"F0.wireOp",EDGE,"E8.33.2"),sQuery(id+"F0.wireOp",EDGE,"E8.33.3"),sQuery(id+"F0.wireOp",EDGE,"E8.34.0"),sQuery(id+"F0.wireOp",EDGE,"E8.34.1"),sQuery(id+"F0.wireOp",EDGE,"E8.34.2"),sQuery(id+"F0.wireOp",EDGE,"E8.34.3"),sQuery(id+"F0.wireOp",EDGE,"E8.35.0"),sQuery(id+"F0.wireOp",EDGE,"E8.35.1"),sQuery(id+"F0.wireOp",EDGE,"E8.35.2"),sQuery(id+"F0.wireOp",EDGE,"E8.35.3")])],"isStart":true});
            var sketch = newSketch(context, id + "F3", { "sketchPlane" : qUnion([Q0])});
            skCircle(sketch, "E130", {"center": v(0, 0) * mm, "radius": 115.22 * mm});
            skCircle(sketch, "E131", {"center": v(0, 0) * mm, "radius": 118.36 * mm});
            skLineSegment(sketch, "E132.1.0", {"start": v(57.6, -99.78) * mm, "end": v(59.18, -102.5) * mm});
            skLineSegment(sketch, "E132.2.0", {"start": v(99.78, -57.6) * mm, "end": v(102.5, -59.18) * mm});
            skLineSegment(sketch, "E132.3.0", {"start": v(115.22, 0) * mm, "end": v(118.36, 0) * mm});
            skLineSegment(sketch, "E132.4.0", {"start": v(99.78, 57.6) * mm, "end": v(102.5, 59.18) * mm});
            skLineSegment(sketch, "E132.5.0", {"start": v(57.6, 99.78) * mm, "end": v(59.18, 102.5) * mm});
            skLineSegment(sketch, "E132.6.0", {"start": v(0, 115.22) * mm, "end": v(0, 118.36) * mm});
            skLineSegment(sketch, "E132.7.0", {"start": v(-57.6, 99.78) * mm, "end": v(-59.18, 102.5) * mm});
            skLineSegment(sketch, "E132.8.0", {"start": v(-99.78, 57.6) * mm, "end": v(-102.5, 59.18) * mm});
            skLineSegment(sketch, "E132.9.0", {"start": v(-115.22, 0) * mm, "end": v(-118.36, 0) * mm});
            skLineSegment(sketch, "E132.10.0", {"start": v(-99.78, -57.6) * mm, "end": v(-102.5, -59.18) * mm});
            skLineSegment(sketch, "E132.11.0", {"start": v(-57.6, -99.78) * mm, "end": v(-59.18, -102.5) * mm});
            skSolve(sketch);
        }
        {
            var Q0;
            {var subQ0=sQuery(id+"F3.wireOp",EDGE,"E132.6.0");Q0=makeQuery(id+"F3.imprint","IMPRINT",FACE,{"disambiguationData":[TD([[makeQuery(id+"F3.imprint","IMPRINT",EDGE,{"derivedFrom":subQ0}),1.0]])]});}
            var Q1;
            {var subQ0=sQuery(id+"F3.wireOp",EDGE,"E132.5.0");Q1=makeQuery(id+"F3.imprint","IMPRINT",FACE,{"disambiguationData":[TD([[makeQuery(id+"F3.imprint","IMPRINT",EDGE,{"derivedFrom":subQ0}),1.0]])]});}
            var Q2;
            {var subQ0=sQuery(id+"F3.wireOp",EDGE,"E132.7.0");Q2=makeQuery(id+"F3.imprint","IMPRINT",FACE,{"disambiguationData":[TD([[makeQuery(id+"F3.imprint","IMPRINT",EDGE,{"derivedFrom":subQ0}),1.0]])]});}
            var Q3;
            {var subQ0=sQuery(id+"F3.wireOp",EDGE,"E132.4.0");Q3=makeQuery(id+"F3.imprint","IMPRINT",FACE,{"disambiguationData":[TD([[makeQuery(id+"F3.imprint","IMPRINT",EDGE,{"derivedFrom":subQ0}),1.0]])]});}
            var Q4;
            {var subQ0=sQuery(id+"F3.wireOp",EDGE,"E132.1.0");Q4=makeQuery(id+"F3.imprint","IMPRINT",FACE,{"disambiguationData":[TD([[makeQuery(id+"F3.imprint","IMPRINT",EDGE,{"derivedFrom":subQ0}),-1.0]])]});}
            extrude(context, id + "F4", {"entities" : qUnion([Q0, Q1, Q2, Q3, Q4]), "operationType" : NewBodyOperationType.REMOVE, "endBound" : BoundingType.SYMMETRIC, "oppositeDirection" : true, "depth" : 25 * mm, "offsetDistance" : 25 * mm});
        }
        {
            var Q0;
            Q0=makeQuery(id+"F2.imprint","IMPRINT",FACE,{"disambiguationData":[TD([[makeQuery(id+"F2.imprint","IMPRINT",EDGE,{"derivedFrom":sQuery(id+"F2.wireOp",EDGE,"E98")}),-1.0]])]});
            var Q1;
            Q1=makeQuery(id+"F2.imprint","IMPRINT",FACE,{"disambiguationData":[TD([[makeQuery(id+"F2.imprint","IMPRINT",EDGE,{"derivedFrom":sQuery(id+"F2.wireOp",EDGE,"E114")}),-1.0]])]});
            var Q2;
            Q2=makeQuery(id+"F2.imprint","IMPRINT",FACE,{"disambiguationData":[TD([[makeQuery(id+"F2.imprint","IMPRINT",EDGE,{"derivedFrom":sQuery(id+"F2.wireOp",EDGE,"E117")}),1.0]])]});
            var Q3;
            {var subQ0=sQuery(id+"F2.wireOp",EDGE,"E126");Q3=makeQuery(id+"F2.imprint","IMPRINT",FACE,{"disambiguationData":[TD([[makeQuery(id+"F2.imprint","IMPRINT",EDGE,{"derivedFrom":subQ0}),1.0]])]});}
            var Q4;
            {var subQ0=sQuery(id+"F2.wireOp",EDGE,"E126");Q4=makeQuery(id+"F2.imprint","IMPRINT",FACE,{"disambiguationData":[TD([[makeQuery(id+"F2.imprint","IMPRINT",EDGE,{"derivedFrom":subQ0}),-1.0]])]});}
            var Q5;
            {var subQ0=sQuery(id+"F2.wireOp",EDGE,"E127.1.0");Q5=makeQuery(id+"F2.imprint","IMPRINT",FACE,{"disambiguationData":[TD([[makeQuery(id+"F2.imprint","IMPRINT",EDGE,{"derivedFrom":subQ0}),-1.0]])]});}
            var Q6;
            {var subQ0=sQuery(id+"F2.wireOp",EDGE,"E127.34.0");Q6=makeQuery(id+"F2.imprint","IMPRINT",FACE,{"disambiguationData":[TD([[makeQuery(id+"F2.imprint","IMPRINT",EDGE,{"derivedFrom":subQ0}),-1.0]])]});}
            var Q7;
            {var subQ4=sQuery(id+"F2.wireOp",EDGE,"E90.MirrorCS");Q7=makeQuery(id+"F2.imprint","IMPRINT",FACE,{"disambiguationData":[TD([[makeQuery(id+"F2.imprint","IMPRINT",EDGE,{"derivedFrom":subQ4}),1.0]])]});}
            var Q8;
            {var subQ1=sQuery(id+"F2.wireOp",EDGE,"E50");Q8=makeQuery(id+"F2.imprint","IMPRINT",FACE,{"disambiguationData":[TD([[makeQuery(id+"F2.imprint","IMPRINT",EDGE,{"derivedFrom":subQ1}),-1.0]])]});}
            var Q9;
            Q9=makeQuery(id+"F2.imprint","IMPRINT",FACE,{"disambiguationData":[TD([[makeQuery(id+"F2.imprint","IMPRINT",EDGE,{"derivedFrom":sQuery(id+"F2.wireOp",EDGE,"E48")}),1.0]])]});
            var Q10;
            Q10=makeQuery(id+"F2.imprint","IMPRINT",FACE,{"disambiguationData":[TD([[makeQuery(id+"F2.imprint","IMPRINT",EDGE,{"derivedFrom":sQuery(id+"F2.wireOp",EDGE,"E13")}),1.0]])]});
            var Q11;
            Q11=makeQuery(id+"F2.imprint","IMPRINT",FACE,{"disambiguationData":[TD([[makeQuery(id+"F2.imprint","IMPRINT",EDGE,{"derivedFrom":sQuery(id+"F2.wireOp",EDGE,"E34")}),-1.0]])]});
            var Q12;
            Q12=makeQuery(id+"F2.imprint","IMPRINT",FACE,{"disambiguationData":[TD([[makeQuery(id+"F2.imprint","IMPRINT",EDGE,{"derivedFrom":sQuery(id+"F2.wireOp",EDGE,"E11")}),1.0]])]});
            var Q13;
            Q13=makeQuery(id+"F2.imprint","IMPRINT",FACE,{"disambiguationData":[TD([[makeQuery(id+"F2.imprint","IMPRINT",EDGE,{"derivedFrom":sQuery(id+"F2.wireOp",EDGE,"E83.MirrorC")}),-1.0]])]});
            var Q14;
            {var subQ3=sQuery(id+"F2.wireOp",EDGE,"E93.MirrorCS");var subQ4=sQuery(id+"F2.wireOp",EDGE,"E52");var subQ5=makeQuery(id+"F2.imprint","INTERSECT",VERTEX,{"derivedFrom":[subQ4,subQ3]});Q14=makeQuery(id+"F2.imprint","IMPRINT",FACE,{"disambiguationData":[TD([[makeQuery(id+"F2.imprint","IMPRINT",EDGE,{"disambiguationData":[TD([[subQ5,-1.0]])],"derivedFrom":subQ4}),1.0]])]});}
            var Q15;
            {var subQ0=sQuery(id+"F2.wireOp",EDGE,"E127.10.0");Q15=makeQuery(id+"F2.imprint","IMPRINT",FACE,{"disambiguationData":[TD([[makeQuery(id+"F2.imprint","IMPRINT",EDGE,{"derivedFrom":subQ0}),-1.0]])]});}
            var Q16;
            {var subQ0=sQuery(id+"F2.wireOp",EDGE,"E10");var subQ4=sQuery(id+"F2.wireOp",EDGE,"E49");var subQ5=makeQuery(id+"F2.imprint","INTERSECT",VERTEX,{"derivedFrom":[subQ0,subQ4]});Q16=makeQuery(id+"F2.imprint","IMPRINT",FACE,{"disambiguationData":[TD([[makeQuery(id+"F2.imprint","IMPRINT",EDGE,{"disambiguationData":[TD([[subQ5,-1.0]])],"derivedFrom":subQ0}),1.0]])]});}
            var Q17;
            {var subQ0=sQuery(id+"F2.wireOp",EDGE,"E125.12.0");Q17=makeQuery(id+"F2.imprint","IMPRINT",FACE,{"disambiguationData":[TD([[makeQuery(id+"F2.imprint","IMPRINT",EDGE,{"derivedFrom":subQ0}),-1.0]])]});}
            var Q18;
            {var subQ5=sQuery(id+"F2.wireOp",EDGE,"E125.12.0");Q18=makeQuery(id+"F2.imprint","IMPRINT",FACE,{"disambiguationData":[TD([[makeQuery(id+"F2.imprint","IMPRINT",EDGE,{"derivedFrom":subQ5}),1.0]])]});}
            var Q19;
            {var subQ0=sQuery(id+"F2.wireOp",EDGE,"E127.11.0");Q19=makeQuery(id+"F2.imprint","IMPRINT",FACE,{"disambiguationData":[TD([[makeQuery(id+"F2.imprint","IMPRINT",EDGE,{"derivedFrom":subQ0}),-1.0]])]});}
            var Q20;
            {var subQ5=sQuery(id+"F2.wireOp",EDGE,"E127.12.0");Q20=makeQuery(id+"F2.imprint","IMPRINT",FACE,{"disambiguationData":[TD([[makeQuery(id+"F2.imprint","IMPRINT",EDGE,{"derivedFrom":subQ5}),-1.0]])]});}
            var Q21;
            {var subQ1=sQuery(id+"F2.wireOp",EDGE,"E10");var subQ3=sQuery(id+"F2.wireOp",EDGE,"E127.13.0");var subQ4=makeQuery(id+"F2.imprint","INTERSECT",VERTEX,{"derivedFrom":[subQ1,subQ3]});Q21=makeQuery(id+"F2.imprint","IMPRINT",FACE,{"disambiguationData":[TD([[makeQuery(id+"F2.imprint","IMPRINT",EDGE,{"disambiguationData":[TD([[subQ4,1.0]])],"derivedFrom":subQ3}),-1.0]])]});}
            var Q22;
            {var subQ5=sQuery(id+"F2.wireOp",EDGE,"E125.13.0");Q22=makeQuery(id+"F2.imprint","IMPRINT",FACE,{"disambiguationData":[TD([[makeQuery(id+"F2.imprint","IMPRINT",EDGE,{"derivedFrom":subQ5}),-1.0]])]});}
            var Q23;
            {var subQ0=sQuery(id+"F2.wireOp",EDGE,"E125.15.0");Q23=makeQuery(id+"F2.imprint","IMPRINT",FACE,{"disambiguationData":[TD([[makeQuery(id+"F2.imprint","IMPRINT",EDGE,{"derivedFrom":subQ0}),1.0]])]});}
            var Q24;
            {var subQ0=sQuery(id+"F2.wireOp",EDGE,"E53");var subQ1=sQuery(id+"F2.wireOp",EDGE,"E52");var subQ2=makeQuery(id+"F2.imprint","INTERSECT",VERTEX,{"derivedFrom":[subQ1,subQ0]});Q24=makeQuery(id+"F2.imprint","IMPRINT",FACE,{"disambiguationData":[TD([[makeQuery(id+"F2.imprint","IMPRINT",EDGE,{"disambiguationData":[TD([[subQ2,1.0]])],"derivedFrom":subQ1}),1.0]])]});}
            var Q25;
            {var subQ4=sQuery(id+"F2.wireOp",EDGE,"E53");var subQ6=sQuery(id+"F2.wireOp",EDGE,"E10");var subQ14=makeQuery(id+"F2.imprint","INTERSECT",VERTEX,{"disambiguationData":[OD(0.0)],"derivedFrom":[subQ6,subQ4]});Q25=makeQuery(id+"F2.imprint","IMPRINT",FACE,{"disambiguationData":[TD([[makeQuery(id+"F2.imprint","IMPRINT",EDGE,{"disambiguationData":[TD([[subQ14,-1.0]])],"derivedFrom":subQ6}),1.0]])]});}
            var Q26;
            {var subQ0=sQuery(id+"F2.wireOp",EDGE,"E125.15.0");Q26=makeQuery(id+"F2.imprint","IMPRINT",FACE,{"disambiguationData":[TD([[makeQuery(id+"F2.imprint","IMPRINT",EDGE,{"derivedFrom":subQ0}),-1.0]])]});}
            var Q27;
            {var subQ0=sQuery(id+"F2.wireOp",EDGE,"E125.16.0");Q27=makeQuery(id+"F2.imprint","IMPRINT",FACE,{"disambiguationData":[TD([[makeQuery(id+"F2.imprint","IMPRINT",EDGE,{"derivedFrom":subQ0}),-1.0]])]});}
            var Q28;
            {var subQ0=sQuery(id+"F2.wireOp",EDGE,"E9");var subQ1=makeQuery(id+"F2.imprint","INTERSECT",VERTEX,{"derivedFrom":[subQ0,sQuery(id+"F2.wireOp",EDGE,"E127.17.0")]});Q28=makeQuery(id+"F2.imprint","IMPRINT",FACE,{"disambiguationData":[TD([[makeQuery(id+"F2.imprint","IMPRINT",EDGE,{"disambiguationData":[TD([[subQ1,1.0]])],"derivedFrom":subQ0}),-1.0]])]});}
            var Q29;
            {var subQ0=sQuery(id+"F2.wireOp",EDGE,"E127.17.0");Q29=makeQuery(id+"F2.imprint","IMPRINT",FACE,{"disambiguationData":[TD([[makeQuery(id+"F2.imprint","IMPRINT",EDGE,{"derivedFrom":subQ0}),1.0]])]});}
            var Q30;
            {var subQ0=sQuery(id+"F2.wireOp",EDGE,"E127.17.0");Q30=makeQuery(id+"F2.imprint","IMPRINT",FACE,{"disambiguationData":[TD([[makeQuery(id+"F2.imprint","IMPRINT",EDGE,{"derivedFrom":subQ0}),-1.0]])]});}
            var Q31;
            {var subQ0=sQuery(id+"F2.wireOp",EDGE,"E125.17.0");Q31=makeQuery(id+"F2.imprint","IMPRINT",FACE,{"disambiguationData":[TD([[makeQuery(id+"F2.imprint","IMPRINT",EDGE,{"derivedFrom":subQ0}),-1.0]])]});}
            var Q32;
            {var subQ3=sQuery(id+"F2.wireOp",EDGE,"E125.19.0");Q32=makeQuery(id+"F2.imprint","IMPRINT",FACE,{"disambiguationData":[TD([[makeQuery(id+"F2.imprint","IMPRINT",EDGE,{"derivedFrom":subQ3}),1.0]])]});}
            var Q33;
            {var subQ0=sQuery(id+"F2.wireOp",EDGE,"E127.19.0");Q33=makeQuery(id+"F2.imprint","IMPRINT",FACE,{"disambiguationData":[TD([[makeQuery(id+"F2.imprint","IMPRINT",EDGE,{"derivedFrom":subQ0}),1.0]])]});}
            var Q34;
            {var subQ0=sQuery(id+"F2.wireOp",EDGE,"E127.19.0");Q34=makeQuery(id+"F2.imprint","IMPRINT",FACE,{"disambiguationData":[TD([[makeQuery(id+"F2.imprint","IMPRINT",EDGE,{"derivedFrom":subQ0}),-1.0]])]});}
            var Q35;
            {var subQ1=sQuery(id+"F2.wireOp",EDGE,"E10");var subQ11=makeQuery(id+"F2.imprint","INTERSECT",VERTEX,{"derivedFrom":[subQ1,sQuery(id+"F2.wireOp",EDGE,"E127.19.0")]});Q35=makeQuery(id+"F2.imprint","IMPRINT",FACE,{"disambiguationData":[TD([[makeQuery(id+"F2.imprint","IMPRINT",EDGE,{"disambiguationData":[TD([[subQ11,1.0]])],"derivedFrom":subQ1}),1.0]])]});}
            var Q36;
            {var subQ0=sQuery(id+"F2.wireOp",EDGE,"E125.19.0");Q36=makeQuery(id+"F2.imprint","IMPRINT",FACE,{"disambiguationData":[TD([[makeQuery(id+"F2.imprint","IMPRINT",EDGE,{"derivedFrom":subQ0}),-1.0]])]});}
            var Q37;
            {var subQ0=sQuery(id+"F2.wireOp",EDGE,"E9");var subQ1=makeQuery(id+"F2.imprint","INTERSECT",VERTEX,{"derivedFrom":[subQ0,sQuery(id+"F2.wireOp",EDGE,"E127.19.0")]});Q37=makeQuery(id+"F2.imprint","IMPRINT",FACE,{"disambiguationData":[TD([[makeQuery(id+"F2.imprint","IMPRINT",EDGE,{"disambiguationData":[TD([[subQ1,1.0]])],"derivedFrom":subQ0}),-1.0]])]});}
            var Q38;
            {var subQ0=sQuery(id+"F2.wireOp",EDGE,"E125.20.0");Q38=makeQuery(id+"F2.imprint","IMPRINT",FACE,{"disambiguationData":[TD([[makeQuery(id+"F2.imprint","IMPRINT",EDGE,{"derivedFrom":subQ0}),-1.0]])]});}
            var Q39;
            {var subQ0=sQuery(id+"F2.wireOp",EDGE,"E125.21.0");Q39=makeQuery(id+"F2.imprint","IMPRINT",FACE,{"disambiguationData":[TD([[makeQuery(id+"F2.imprint","IMPRINT",EDGE,{"derivedFrom":subQ0}),-1.0]])]});}
            var Q40;
            {var subQ0=sQuery(id+"F2.wireOp",EDGE,"E94.MirrorCS");var subQ1=sQuery(id+"F2.wireOp",EDGE,"E93.MirrorCS");var subQ2=makeQuery(id+"F2.imprint","INTERSECT",VERTEX,{"derivedFrom":[subQ1,subQ0]});Q40=makeQuery(id+"F2.imprint","IMPRINT",FACE,{"disambiguationData":[TD([[makeQuery(id+"F2.imprint","IMPRINT",EDGE,{"disambiguationData":[TD([[subQ2,1.0]])],"derivedFrom":subQ1}),-1.0]])]});}
            var Q41;
            {var subQ5=sQuery(id+"F2.wireOp",EDGE,"E125.23.0");Q41=makeQuery(id+"F2.imprint","IMPRINT",FACE,{"disambiguationData":[TD([[makeQuery(id+"F2.imprint","IMPRINT",EDGE,{"derivedFrom":subQ5}),1.0]])]});}
            var Q42;
            {var subQ1=sQuery(id+"F2.wireOp",EDGE,"E10");var subQ3=sQuery(id+"F2.wireOp",EDGE,"E127.23.0");var subQ4=makeQuery(id+"F2.imprint","INTERSECT",VERTEX,{"derivedFrom":[subQ1,subQ3]});Q42=makeQuery(id+"F2.imprint","IMPRINT",FACE,{"disambiguationData":[TD([[makeQuery(id+"F2.imprint","IMPRINT",EDGE,{"disambiguationData":[TD([[subQ4,1.0]])],"derivedFrom":subQ3}),1.0]])]});}
            var Q43;
            {var subQ0=sQuery(id+"F2.wireOp",EDGE,"E127.24.0");Q43=makeQuery(id+"F2.imprint","IMPRINT",FACE,{"disambiguationData":[TD([[makeQuery(id+"F2.imprint","IMPRINT",EDGE,{"derivedFrom":subQ0}),1.0]])]});}
            var Q44;
            {var subQ0=sQuery(id+"F2.wireOp",EDGE,"E10");var subQ8=makeQuery(id+"F2.imprint","INTERSECT",VERTEX,{"derivedFrom":[subQ0,sQuery(id+"F2.wireOp",EDGE,"E127.23.0")]});Q44=makeQuery(id+"F2.imprint","IMPRINT",FACE,{"disambiguationData":[TD([[makeQuery(id+"F2.imprint","IMPRINT",EDGE,{"disambiguationData":[TD([[subQ8,-1.0]])],"derivedFrom":subQ0}),1.0]])]});}
            var Q45;
            {var subQ0=sQuery(id+"F2.wireOp",EDGE,"E125.23.0");Q45=makeQuery(id+"F2.imprint","IMPRINT",FACE,{"disambiguationData":[TD([[makeQuery(id+"F2.imprint","IMPRINT",EDGE,{"derivedFrom":subQ0}),-1.0]])]});}
            var Q46;
            {var subQ0=sQuery(id+"F2.wireOp",EDGE,"E127.24.0");Q46=makeQuery(id+"F2.imprint","IMPRINT",FACE,{"disambiguationData":[TD([[makeQuery(id+"F2.imprint","IMPRINT",EDGE,{"derivedFrom":subQ0}),-1.0]])]});}
            var Q47;
            {var subQ5=sQuery(id+"F2.wireOp",EDGE,"E125.24.0");Q47=makeQuery(id+"F2.imprint","IMPRINT",FACE,{"disambiguationData":[TD([[makeQuery(id+"F2.imprint","IMPRINT",EDGE,{"derivedFrom":subQ5}),-1.0]])]});}
            var Q48;
            {var subQ0=sQuery(id+"F2.wireOp",EDGE,"E127.25.0");Q48=makeQuery(id+"F2.imprint","IMPRINT",FACE,{"disambiguationData":[TD([[makeQuery(id+"F2.imprint","IMPRINT",EDGE,{"derivedFrom":subQ0}),-1.0]])]});}
            var Q49;
            {var subQ3=sQuery(id+"F2.wireOp",EDGE,"E127.26.0");Q49=makeQuery(id+"F2.imprint","IMPRINT",FACE,{"disambiguationData":[TD([[makeQuery(id+"F2.imprint","IMPRINT",EDGE,{"derivedFrom":subQ3}),-1.0]])]});}
            var Q50;
            {var subQ0=sQuery(id+"F2.wireOp",EDGE,"E127.27.0");Q50=makeQuery(id+"F2.imprint","IMPRINT",FACE,{"disambiguationData":[TD([[makeQuery(id+"F2.imprint","IMPRINT",EDGE,{"derivedFrom":subQ0}),-1.0]])]});}
            var Q51;
            {var subQ0=sQuery(id+"F2.wireOp",EDGE,"E127.9.0");Q51=makeQuery(id+"F2.imprint","IMPRINT",FACE,{"disambiguationData":[TD([[makeQuery(id+"F2.imprint","IMPRINT",EDGE,{"derivedFrom":subQ0}),-1.0]])]});}
            var Q52;
            {var subQ0=sQuery(id+"F2.wireOp",EDGE,"E127.8.0");Q52=makeQuery(id+"F2.imprint","IMPRINT",FACE,{"disambiguationData":[TD([[makeQuery(id+"F2.imprint","IMPRINT",EDGE,{"derivedFrom":subQ0}),-1.0]])]});}
            var Q53;
            {var subQ0=sQuery(id+"F2.wireOp",EDGE,"E127.4.0");Q53=makeQuery(id+"F2.imprint","IMPRINT",FACE,{"disambiguationData":[TD([[makeQuery(id+"F2.imprint","IMPRINT",EDGE,{"derivedFrom":subQ0}),-1.0]])]});}
            var Q54;
            {var subQ0=sQuery(id+"F2.wireOp",EDGE,"E127.5.0");Q54=makeQuery(id+"F2.imprint","IMPRINT",FACE,{"disambiguationData":[TD([[makeQuery(id+"F2.imprint","IMPRINT",EDGE,{"derivedFrom":subQ0}),-1.0]])]});}
            var Q55;
            {var subQ0=sQuery(id+"F2.wireOp",EDGE,"E127.31.0");Q55=makeQuery(id+"F2.imprint","IMPRINT",FACE,{"disambiguationData":[TD([[makeQuery(id+"F2.imprint","IMPRINT",EDGE,{"derivedFrom":subQ0}),-1.0]])]});}
            var Q56;
            {var subQ0=sQuery(id+"F2.wireOp",EDGE,"E127.30.0");Q56=makeQuery(id+"F2.imprint","IMPRINT",FACE,{"disambiguationData":[TD([[makeQuery(id+"F2.imprint","IMPRINT",EDGE,{"derivedFrom":subQ0}),-1.0]])]});}
            var Q57;
            {var subQ0=sQuery(id+"F2.wireOp",EDGE,"E125.1.0");Q57=makeQuery(id+"F2.imprint","IMPRINT",FACE,{"disambiguationData":[TD([[makeQuery(id+"F2.imprint","IMPRINT",EDGE,{"derivedFrom":subQ0}),-1.0]])]});}
            var Q58;
            {var subQ0=sQuery(id+"F2.wireOp",EDGE,"E125.2.0");Q58=makeQuery(id+"F2.imprint","IMPRINT",FACE,{"disambiguationData":[TD([[makeQuery(id+"F2.imprint","IMPRINT",EDGE,{"derivedFrom":subQ0}),-1.0]])]});}
            var Q59;
            {var subQ0=sQuery(id+"F2.wireOp",EDGE,"E125.3.0");Q59=makeQuery(id+"F2.imprint","IMPRINT",FACE,{"disambiguationData":[TD([[makeQuery(id+"F2.imprint","IMPRINT",EDGE,{"derivedFrom":subQ0}),-1.0]])]});}
            var Q60;
            {var subQ0=sQuery(id+"F2.wireOp",EDGE,"E125.4.0");Q60=makeQuery(id+"F2.imprint","IMPRINT",FACE,{"disambiguationData":[TD([[makeQuery(id+"F2.imprint","IMPRINT",EDGE,{"derivedFrom":subQ0}),-1.0]])]});}
            var Q61;
            {var subQ0=sQuery(id+"F2.wireOp",EDGE,"E125.34.0");Q61=makeQuery(id+"F2.imprint","IMPRINT",FACE,{"disambiguationData":[TD([[makeQuery(id+"F2.imprint","IMPRINT",EDGE,{"derivedFrom":subQ0}),-1.0]])]});}
            var Q62;
            {var subQ0=sQuery(id+"F2.wireOp",EDGE,"E125.33.0");Q62=makeQuery(id+"F2.imprint","IMPRINT",FACE,{"disambiguationData":[TD([[makeQuery(id+"F2.imprint","IMPRINT",EDGE,{"derivedFrom":subQ0}),-1.0]])]});}
            var Q63;
            {var subQ0=sQuery(id+"F2.wireOp",EDGE,"E125.32.0");Q63=makeQuery(id+"F2.imprint","IMPRINT",FACE,{"disambiguationData":[TD([[makeQuery(id+"F2.imprint","IMPRINT",EDGE,{"derivedFrom":subQ0}),-1.0]])]});}
            var Q64;
            {var subQ0=sQuery(id+"F2.wireOp",EDGE,"E125.31.0");Q64=makeQuery(id+"F2.imprint","IMPRINT",FACE,{"disambiguationData":[TD([[makeQuery(id+"F2.imprint","IMPRINT",EDGE,{"derivedFrom":subQ0}),-1.0]])]});}
            var Q65;
            {var subQ0=sQuery(id+"F2.wireOp",EDGE,"E125.8.0");Q65=makeQuery(id+"F2.imprint","IMPRINT",FACE,{"disambiguationData":[TD([[makeQuery(id+"F2.imprint","IMPRINT",EDGE,{"derivedFrom":subQ0}),-1.0]])]});}
            var Q66;
            {var subQ0=sQuery(id+"F2.wireOp",EDGE,"E125.7.0");Q66=makeQuery(id+"F2.imprint","IMPRINT",FACE,{"disambiguationData":[TD([[makeQuery(id+"F2.imprint","IMPRINT",EDGE,{"derivedFrom":subQ0}),-1.0]])]});}
            var Q67;
            {var subQ0=sQuery(id+"F2.wireOp",EDGE,"E125.28.0");Q67=makeQuery(id+"F2.imprint","IMPRINT",FACE,{"disambiguationData":[TD([[makeQuery(id+"F2.imprint","IMPRINT",EDGE,{"derivedFrom":subQ0}),-1.0]])]});}
            var Q68;
            {var subQ0=sQuery(id+"F2.wireOp",EDGE,"E125.27.0");Q68=makeQuery(id+"F2.imprint","IMPRINT",FACE,{"disambiguationData":[TD([[makeQuery(id+"F2.imprint","IMPRINT",EDGE,{"derivedFrom":subQ0}),-1.0]])]});}
            extrude(context, id + "F5", {"entities" : qUnion([Q0, Q1, Q2, Q3, Q4, Q5, Q6, Q7, Q8, Q9, Q10, Q11, Q12, Q13, Q14, Q15, Q16, Q17, Q18, Q19, Q20, Q21, Q22, Q23, Q24, Q25, Q26, Q27, Q28, Q29, Q30, Q31, Q32, Q33, Q34, Q35, Q36, Q37, Q38, Q39, Q40, Q41, Q42, Q43, Q44, Q45, Q46, Q47, Q48, Q49, Q50, Q51, Q52, Q53, Q54, Q55, Q56, Q57, Q58, Q59, Q60, Q61, Q62, Q63, Q64, Q65, Q66, Q67, Q68]), "operationType" : NewBodyOperationType.REMOVE, "endBound" : BoundingType.SYMMETRIC, "oppositeDirection" : true, "depth" : 25 * mm, "offsetDistance" : 25 * mm});
        }
    });
